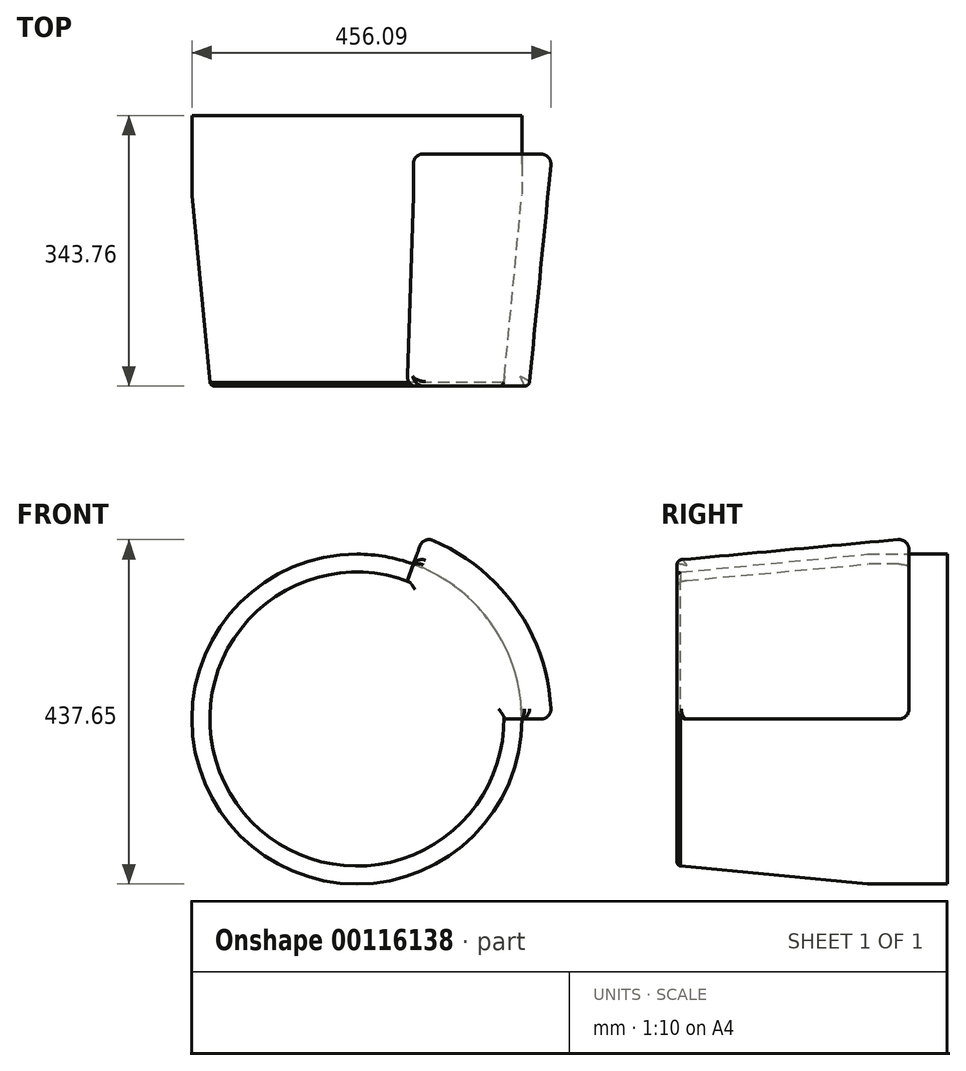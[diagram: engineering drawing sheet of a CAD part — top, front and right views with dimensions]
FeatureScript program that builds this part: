
annotation { "Feature Type Name" : "Feature", "Feature Type Description" : "" }
export const myFeature = defineFeature(function(context is Context, id is Id, definition is map)
    precondition{}
    {
        {
            var Q0;
            Q0=qCreatedBy(makeId("Top.planeOp"),FACE);
            var sketch = newSketch(context, id + "F0", { "sketchPlane" : qUnion([Q0])});
            skLineSegment(sketch, "E0", {"start": v(209.55, 106.1) * mm, "end": v(209.55, 4.8) * mm});
            skLineSegment(sketch, "E1", {"start": v(180.63, -237.66) * mm, "end": v(0, -237.66) * mm});
            skLineSegment(sketch, "E2", {"start": v(209.55, 106.1) * mm, "end": v(0, 106.1) * mm});
            skArc(sketch, "E3.filletArc", {"start": v(180.63, -237.66) * mm, "mid": v(184.5, -236.34) * mm, "end": v(186.76, -232.95) * mm});
            skLineSegment(sketch, "E4", {"start": v(0, 106.1) * mm, "end": v(0, -237.66) * mm});
            skLineSegment(sketch, "E5", {"start": v(186.76, -232.95) * mm, "end": v(209.52, 4.2) * mm});
            skPoint(sketch, "E6.visualSharp", {"position": v(209.55, 4.5) * mm});
            skArc(sketch, "E6.filletArc", {"start": v(209.52, 4.2) * mm, "mid": v(209.54, 4.5) * mm, "end": v(209.55, 4.8) * mm});
            skLineSegment(sketch, "E7", {"start": v(240, -26.35) * mm, "end": v(219.8, -231.93) * mm});
            skLineSegment(sketch, "E8", {"start": v(213.47, -237.66) * mm, "end": v(180.63, -237.66) * mm});
            skPoint(sketch, "E9.visualSharp", {"position": v(219.23, -237.66) * mm});
            skArc(sketch, "E9.filletArc", {"start": v(213.47, -237.66) * mm, "mid": v(217.74, -236.01) * mm, "end": v(219.8, -231.93) * mm});
            skPoint(sketch, "E10.visualSharp", {"position": v(241.37, -12.4) * mm});
            skLineSegment(sketch, "E11", {"start": v(240, -26.35) * mm, "end": v(246.83, 43.1) * mm});
            skLineSegment(sketch, "E12", {"start": v(234.19, 57.03) * mm, "end": v(209.55, 57.03) * mm});
            skPoint(sketch, "E12.endSnap0", {"position": v(209.55, 55.45) * mm});
            skPoint(sketch, "E13.visualSharp", {"position": v(248.2, 57.03) * mm});
            skArc(sketch, "E13.filletArc", {"start": v(246.83, 43.1) * mm, "mid": v(243.6, 52.86) * mm, "end": v(234.19, 57.03) * mm});
            skSolve(sketch);
        }
        {
            var Q0;
            Q0=makeQuery(id+"F0.imprint","IMPRINT",FACE,{"disambiguationData":[TD([[makeQuery(id+"F0.imprint","IMPRINT",EDGE,{"derivedFrom":sQuery(id+"F0.wireOp",EDGE,"E0")}),-1.0]])]});
            var Q1;
            Q1=sQuery(id+"F0.wireOp",EDGE,"E4");
            revolve(context, id + "F1", {"entities" : qUnion([Q0]), "axis" : qUnion([Q1]), "revolveType" : RevolveType.FULL});
        }
        {
            var Q0;
            {var subQ2=sQuery(id+"F0.wireOp",EDGE,"E3.filletArc");Q0=makeQuery(id+"F0.imprint","IMPRINT",FACE,{"disambiguationData":[TD([[makeQuery(id+"F0.imprint","IMPRINT",EDGE,{"derivedFrom":subQ2}),-1.0]])]});}
            var Q1;
            Q1=sQuery(id+"F0.wireOp",EDGE,"E4");
            revolve(context, id + "F2", {"operationType" : NewBodyOperationType.ADD, "entities" : qUnion([Q0]), "axis" : qUnion([Q1]), "revolveType" : RevolveType.ONE_DIRECTION, "angle" : 70 * degree});
        }
        {
            var Q0;
            Q0=makeQuery(id+"F2.opRevolve","CAP_EDGE",EDGE,{"disambiguationData":[OSD([sQuery(id+"F0.wireOp",EDGE,"E7")])],"isStart":true});
            fillet(context, id + "F3", {"entities" : qUnion([Q0]), "radius" : 12.7 * mm, "tangentPropagation" : true, "allowEdgeOverflow" : false});
        }
        {
            var Q0;
            Q0=makeQuery(id+"F2.opRevolve","CAP_EDGE",EDGE,{"disambiguationData":[OSD([sQuery(id+"F0.wireOp",EDGE,"E7")])],"isStart":false});
            fillet(context, id + "F4", {"entities" : qUnion([Q0]), "radius" : 12.7 * mm, "tangentPropagation" : true, "allowEdgeOverflow" : false});
        }
    });
